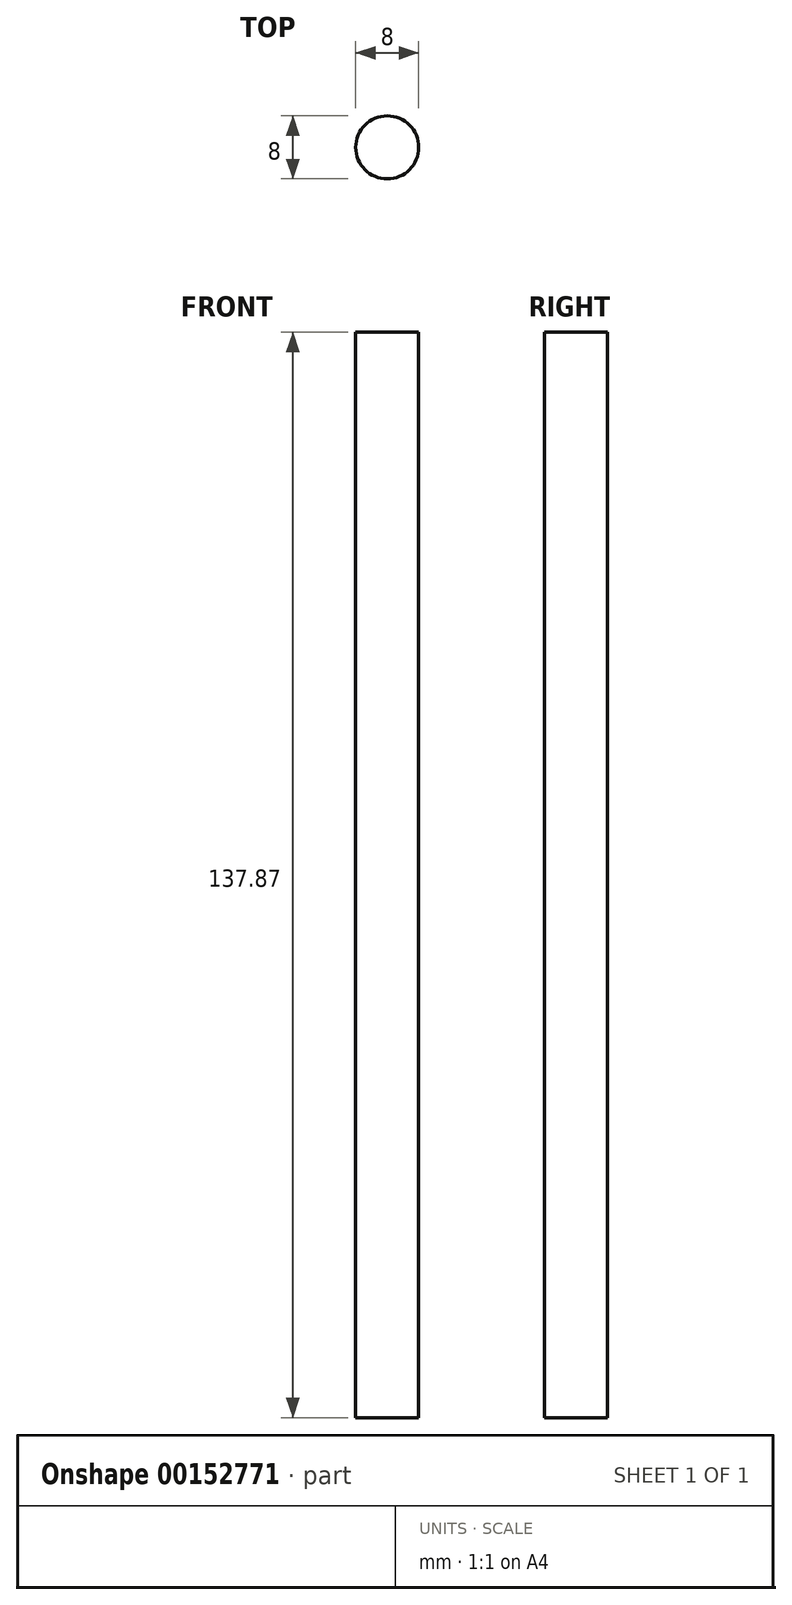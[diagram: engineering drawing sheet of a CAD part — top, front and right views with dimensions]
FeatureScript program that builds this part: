
annotation { "Feature Type Name" : "Feature", "Feature Type Description" : "" }
export const myFeature = defineFeature(function(context is Context, id is Id, definition is map)
    precondition{}
    {
        {
            var Q0;
            Q0=qCreatedBy(makeId("Top.planeOp"),FACE);
            var sketch = newSketch(context, id + "F0", { "sketchPlane" : qUnion([Q0])});
            skCircle(sketch, "E0", {"center": v(0, 0) * mm, "radius": 4 * mm});
            skSolve(sketch);
        }
        {
            var Q0;
            Q0=qSketchRegion(id+"F0",true);
            extrude(context, id + "F1", {"entities" : qUnion([Q0]), "depth" : 137.87 * mm});
        }
    });
